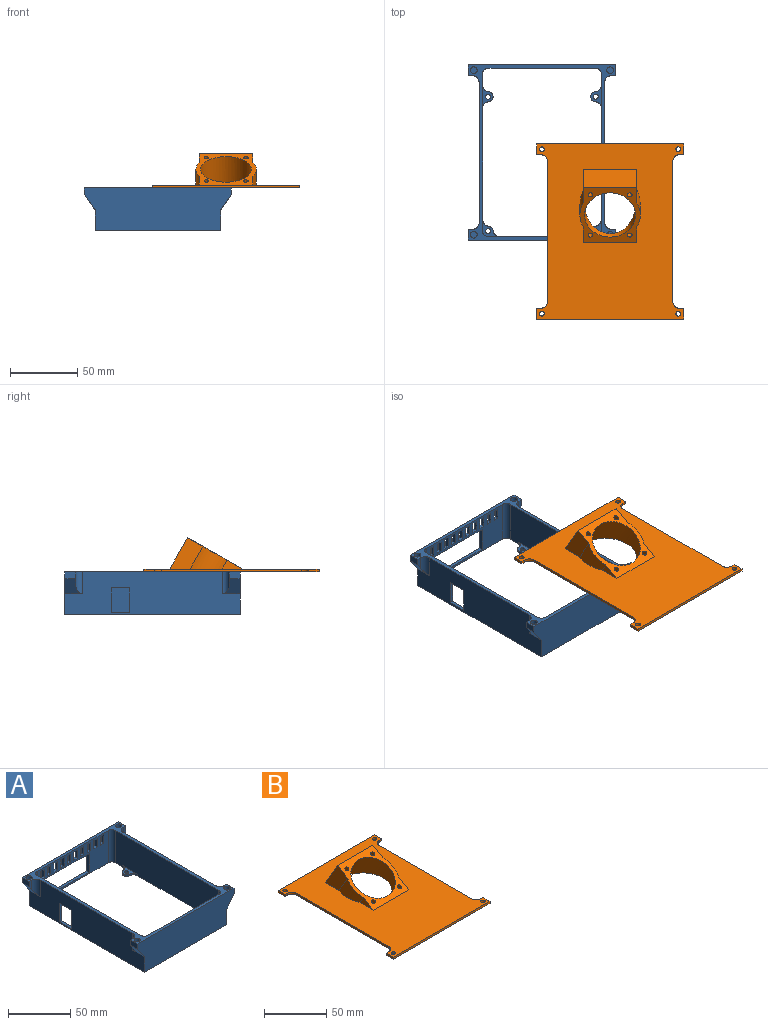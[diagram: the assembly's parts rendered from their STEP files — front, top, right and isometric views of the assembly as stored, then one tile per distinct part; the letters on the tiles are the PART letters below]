
ASSEMBLY  parts=2 mates=1
PART A: 106 faces, bbox 109.6x130.6x31.7 mm
  f0: plane 109.6x31.7mm, normal (0,1,0), area 1821.2mm2, adj f2,f3,f8,f9,f10,f13,f15,f16
  f1: plane 80.4x31.7mm, normal (0,-1,0), area 1231.3mm2, adj f8,f9,f10,f13,f15,f16,f62,f65
  f2: plane 130.6x31.7mm, normal (-1,0,0), area 3458.2mm2, adj f0,f6,f7,f9,f12,f14,f15,f20
  f3: plane 130.6x31.7mm, normal (1,0,0), area 3713mm2, adj f0,f9,f12,f15,f43,f53,f59,f61
  f4: plane 80.4x31.7mm, normal (0,1,0), area 2522.3mm2, adj f9,f15,f23,f26,f35,f37,f63,f64
  f5: plane 117.4x31.7mm, normal (1,0,0), area 3427.5mm2, adj f6,f7,f9,f14,f15,f19,f20,f23
  f6: plane 18.2x2.6mm, normal (0,-1,0), area 47.3mm2, adj f2,f5,f14,f20
  f7: plane 18.2x2.6mm, normal (0,1,0), area 47.3mm2, adj f2,f5,f14,f20
  f8: plane 18.2x2.6mm, normal (1,0,0), area 47.3mm2, adj f0,f1,f13,f16
  f9: plane 130.6x109.6mm, normal (0,0,1), area 1351.5mm2, adj f0,f1,f2,f3,f4,f5,f11,f12
  f10: plane 18.2x2.6mm, normal (-1,0,0), area 47.3mm2, adj f0,f1,f13,f16
  f11: plane 117.4x31.7mm, normal (-1,0,0), area 3682.3mm2, adj f9,f15,f26,f29,f30,f31,f34,f62
  f12: plane 109.6x31.7mm, normal (0,-1,0), area 3138.5mm2, adj f2,f3,f9,f15,f48,f49,f53,f54
  f13: plane 54.8x2.6mm, normal (0,0,-1), area 142.5mm2, adj f0,f1,f8,f10
  f14: plane 14x2.6mm, normal (0,0,-1), area 36.4mm2, adj f2,f5,f6,f7
  f15: plane 130.6x93.6mm, normal (0,0,-1), area 1366.8mm2, adj f0,f1,f2,f3,f4,f5,f11,f12
  f16: plane 54.8x2.6mm, normal (0,0,1), area 142.5mm2, adj f0,f1,f8,f10
  f17: cylinder r=3.75mm len=7.46mm, axis (0,0,-1), area 16.5mm2, adj f15,f19,f32,f33
  f18: cylinder r=1.85mm len=3.7mm, axis (0,0,-1), area 17.4mm2, adj f15,f19
  f19: plane 17.41x7.85mm, normal (0,0,1), area 52.4mm2, adj f5,f17,f18,f32,f33
  f20: plane 14x2.6mm, normal (0,0,1), area 36.4mm2, adj f2,f5,f6,f7
  f21: cylinder r=3.75mm len=3.34mm, axis (0,0,-1), area 7.7mm2, adj f15,f23,f36,f37
  f22: cylinder r=1.85mm len=3.7mm, axis (0,0,-1), area 17.4mm2, adj f15,f23
  f23: plane 12.8x12.8mm, normal (0,0,1), area 54.7mm2, adj f4,f5,f21,f22,f36,f37,f64
  f24: cylinder r=3.75mm len=3.34mm, axis (0,0,-1), area 7.7mm2, adj f15,f26,f34,f35
  f25: cylinder r=1.85mm len=3.7mm, axis (0,0,-1), area 17.4mm2, adj f15,f26
  f26: plane 12.8x12.8mm, normal (0,0,1), area 54.7mm2, adj f4,f11,f24,f25,f34,f35,f63
  f27: cylinder r=3.75mm len=7.46mm, axis (0,0,-1), area 16.5mm2, adj f15,f29,f30,f31
  f28: cylinder r=1.85mm len=3.7mm, axis (0,0,-1), area 17.4mm2, adj f15,f29
  f29: plane 17.41x7.85mm, normal (0,0,1), area 52.4mm2, adj f11,f27,f28,f30,f31
  f30: cylinder r=5mm len=4.97mm, axis (0,0,-1), area 11mm2, adj f11,f15,f27,f29
  f31: cylinder r=5mm len=4.97mm, axis (0,0,-1), area 11mm2, adj f11,f15,f27,f29
  f32: cylinder r=5mm len=4.97mm, axis (0,0,-1), area 11mm2, adj f5,f15,f17,f19
  f33: cylinder r=5mm len=4.97mm, axis (0,0,-1), area 11mm2, adj f5,f15,f17,f19
  f34: cylinder r=5mm len=4.97mm, axis (0,0,-1), area 11mm2, adj f11,f15,f24,f26
  f35: cylinder r=5mm len=4.97mm, axis (0,0,-1), area 11mm2, adj f4,f15,f24,f26
  f36: cylinder r=5mm len=4.97mm, axis (0,0,-1), area 11mm2, adj f5,f15,f21,f23
  f37: cylinder r=5mm len=4.97mm, axis (0,0,-1), area 11mm2, adj f4,f15,f21,f23
  f38: plane 13x11.43mm, normal (-0.82,0,-0.57), area 120.9mm2, adj f0,f2,f39,f40,f60
  f39: plane 8x5mm, normal (-1,0,0), area 40mm2, adj f0,f9,f38,f40
  f40: plane 9.28x3mm, normal (0,-1,0), area 21.4mm2, adj f9,f38,f39,f60
  f41: cylinder r=2.5mm len=6mm, axis (0,0,1), area 94.2mm2, adj f9,f42
  f42: plane 5x5mm, normal (0,0,1), area 19.6mm2, adj f41
  f43: plane 13x11.43mm, normal (0.82,0,-0.57), area 120.9mm2, adj f0,f3,f44,f45,f61
  f44: plane 8x5mm, normal (1,0,0), area 40mm2, adj f0,f9,f43,f45
  f45: plane 9.28x3mm, normal (0,-1,0), area 21.4mm2, adj f9,f43,f44,f61
  f46: cylinder r=2.5mm len=6mm, axis (0,0,1), area 94.2mm2, adj f9,f47
  f47: plane 5x5mm, normal (0,0,1), area 19.6mm2, adj f46
  f48: plane 13x11.43mm, normal (-0.82,0,-0.57), area 120.9mm2, adj f2,f12,f49,f50,f58
  f49: plane 8x5mm, normal (-1,0,0), area 40mm2, adj f9,f12,f48,f50
  f50: plane 9.28x3mm, normal (0,1,0), area 21.4mm2, adj f9,f48,f49,f58
  f51: cylinder r=2.5mm len=6mm, axis (0,0,1), area 94.2mm2, adj f9,f52
  f52: plane 5x5mm, normal (0,0,1), area 19.6mm2, adj f51
  f53: plane 13x11.43mm, normal (0.82,0,-0.57), area 120.9mm2, adj f3,f12,f54,f55,f59
  f54: plane 8x5mm, normal (1,0,0), area 40mm2, adj f9,f12,f53,f55
  f55: plane 9.28x3mm, normal (0,1,0), area 21.4mm2, adj f9,f53,f54,f59
  f56: cylinder r=2.5mm len=6mm, axis (0,0,1), area 94.2mm2, adj f9,f57
  f57: plane 5x5mm, normal (0,0,1), area 19.6mm2, adj f56
  f58: cylinder r=5mm len=16.43mm, axis (0,0,1), area 108.6mm2, adj f2,f9,f48,f50
  f59: cylinder r=5mm len=16.43mm, axis (0,0,1), area 108.6mm2, adj f3,f9,f53,f55
  f60: cylinder r=5mm len=16.43mm, axis (0,0,1), area 108.6mm2, adj f2,f9,f38,f40
  f61: cylinder r=5mm len=16.43mm, axis (0,0,1), area 108.6mm2, adj f3,f9,f43,f45
  f62: cylinder r=4mm len=31.7mm, axis (0,0,1), area 199.2mm2, adj f1,f9,f11,f15
  f63: cylinder r=4mm len=30.2mm, axis (0,0,1), area 189.8mm2, adj f4,f9,f11,f26
  f64: cylinder r=4mm len=30.2mm, axis (0,0,1), area 189.8mm2, adj f4,f5,f9,f23
  f65: cylinder r=4mm len=31.7mm, axis (0,0,1), area 199.2mm2, adj f1,f5,f9,f15
  f66: plane 8x2.6mm, normal (-1,0,0), area 20.8mm2, adj f0,f1,f67,f69
  f67: plane 4x2.6mm, normal (0,0,1), area 10.4mm2, adj f0,f1,f66,f68
  f68: plane 8x2.6mm, normal (1,0,0), area 20.8mm2, adj f0,f1,f67,f69
  f69: plane 4x2.6mm, normal (0,0,-1), area 10.4mm2, adj f0,f1,f66,f68
  f70: plane 8x2.6mm, normal (-1,0,0), area 20.8mm2, adj f0,f1,f71,f73
  f71: plane 4x2.6mm, normal (0,0,1), area 10.4mm2, adj f0,f1,f70,f72
  f72: plane 8x2.6mm, normal (1,0,0), area 20.8mm2, adj f0,f1,f71,f73
  f73: plane 4x2.6mm, normal (0,0,-1), area 10.4mm2, adj f0,f1,f70,f72
  f74: plane 8x2.6mm, normal (-1,0,0), area 20.8mm2, adj f0,f1,f75,f77
  f75: plane 4x2.6mm, normal (0,0,1), area 10.4mm2, adj f0,f1,f74,f76
  f76: plane 8x2.6mm, normal (1,0,0), area 20.8mm2, adj f0,f1,f75,f77
  f77: plane 4x2.6mm, normal (0,0,-1), area 10.4mm2, adj f0,f1,f74,f76
  f78: plane 4x2.6mm, normal (0,0,1), area 10.4mm2, adj f0,f1,f79,f81
  f79: plane 8x2.6mm, normal (1,0,0), area 20.8mm2, adj f0,f1,f78,f80
  f80: plane 4x2.6mm, normal (0,0,-1), area 10.4mm2, adj f0,f1,f79,f81
  f81: plane 8x2.6mm, normal (-1,0,0), area 20.8mm2, adj f0,f1,f78,f80
  f82: plane 8x2.6mm, normal (-1,0,0), area 20.8mm2, adj f0,f1,f83,f85
  f83: plane 4x2.6mm, normal (0,0,1), area 10.4mm2, adj f0,f1,f82,f84
  f84: plane 8x2.6mm, normal (1,0,0), area 20.8mm2, adj f0,f1,f83,f85
  f85: plane 4x2.6mm, normal (0,0,-1), area 10.4mm2, adj f0,f1,f82,f84
  f86: plane 8x2.6mm, normal (-1,0,0), area 20.8mm2, adj f0,f1,f87,f89
  f87: plane 4x2.6mm, normal (0,0,1), area 10.4mm2, adj f0,f1,f86,f88
  f88: plane 8x2.6mm, normal (1,0,0), area 20.8mm2, adj f0,f1,f87,f89
  f89: plane 4x2.6mm, normal (0,0,-1), area 10.4mm2, adj f0,f1,f86,f88
  f90: plane 8x2.6mm, normal (-1,0,0), area 20.8mm2, adj f0,f1,f91,f93
  f91: plane 4x2.6mm, normal (0,0,1), area 10.4mm2, adj f0,f1,f90,f92
  f92: plane 8x2.6mm, normal (1,0,0), area 20.8mm2, adj f0,f1,f91,f93
  f93: plane 4x2.6mm, normal (0,0,-1), area 10.4mm2, adj f0,f1,f90,f92
  f94: plane 8x2.6mm, normal (-1,0,0), area 20.8mm2, adj f0,f1,f95,f97
  f95: plane 4x2.6mm, normal (0,0,1), area 10.4mm2, adj f0,f1,f94,f96
  f96: plane 8x2.6mm, normal (1,0,0), area 20.8mm2, adj f0,f1,f95,f97
  f97: plane 4x2.6mm, normal (0,0,-1), area 10.4mm2, adj f0,f1,f94,f96
  f98: plane 8x2.6mm, normal (-1,0,0), area 20.8mm2, adj f0,f1,f99,f101
  f99: plane 4x2.6mm, normal (0,0,1), area 10.4mm2, adj f0,f1,f98,f100
  f100: plane 8x2.6mm, normal (1,0,0), area 20.8mm2, adj f0,f1,f99,f101
  f101: plane 4x2.6mm, normal (0,0,-1), area 10.4mm2, adj f0,f1,f98,f100
  f102: plane 8x2.6mm, normal (-1,0,0), area 20.8mm2, adj f0,f1,f103,f105
  f103: plane 4x2.6mm, normal (0,0,1), area 10.4mm2, adj f0,f1,f102,f104
  f104: plane 8x2.6mm, normal (1,0,0), area 20.8mm2, adj f0,f1,f103,f105
  f105: plane 4x2.6mm, normal (0,0,-1), area 10.4mm2, adj f0,f1,f102,f104
PART B: 39 faces, bbox 109.6x130.6x44.6 mm
  f0: plane 130.6x109.6mm, normal (0,0,-1), area 11141mm2, adj f5,f6,f7,f8,f9,f10,f11,f12
  f1: plane 45x40.64mm, normal (0,-0.5,0.87), area 774mm2, adj f2,f3,f4,f25,f26,f27,f28,f29
  f2: plane 130.6x109.6mm, normal (0,0,1), area 10215.3mm2, adj f1,f3,f4,f5,f6,f7,f8,f9
  f3: plane 15.19x6.58mm, normal (1,0,0), area 50mm2, adj f1,f2,f28
  f4: plane 15.19x6.58mm, normal (-1,0,0), area 50mm2, adj f1,f2,f29
  f5: plane 8x2mm, normal (1,0,0), area 16mm2, adj f0,f2,f6,f24
  f6: plane 109.6x2mm, normal (0,1,0), area 219.2mm2, adj f0,f2,f5,f7
  f7: plane 8x2mm, normal (-1,0,0), area 16mm2, adj f0,f2,f6,f8
  f8: plane 3x2mm, normal (0,-1,0), area 6mm2, adj f0,f2,f7,f9
  f9: cylinder r=5mm len=5mm, axis (0,0,-1), area 15.7mm2, adj f0,f2,f8,f10
  f10: plane 104.6x2mm, normal (-1,0,0), area 209.2mm2, adj f0,f2,f9,f11
  f11: cylinder r=5mm len=5mm, axis (0,0,-1), area 15.7mm2, adj f0,f2,f10,f12
  f12: plane 3x2mm, normal (0,1,0), area 6mm2, adj f0,f2,f11,f13
  f13: plane 8x2mm, normal (-1,0,0), area 16mm2, adj f0,f2,f12,f14
  f14: plane 109.6x2mm, normal (0,-1,0), area 219.2mm2, adj f0,f2,f13,f15
  f15: plane 8x2mm, normal (1,0,0), area 16mm2, adj f0,f2,f14,f16
  f16: plane 3x2mm, normal (0,1,0), area 6mm2, adj f0,f2,f15,f17
  f17: cylinder r=5mm len=5mm, axis (0,0,-1), area 15.7mm2, adj f0,f2,f16,f18
  f18: plane 104.6x2mm, normal (1,0,0), area 209.2mm2, adj f0,f2,f17,f19
  f19: cylinder r=5mm len=5mm, axis (0,0,-1), area 15.7mm2, adj f0,f2,f18,f24
  f20: cylinder r=1.75mm len=3.5mm, axis (0,0,-1), area 22mm2, adj f0,f2
  f21: cylinder r=1.75mm len=3.5mm, axis (0,0,-1), area 22mm2, adj f0,f2
  f22: cylinder r=1.75mm len=3.5mm, axis (0,0,-1), area 22mm2, adj f0,f2
  f23: cylinder r=1.75mm len=3.5mm, axis (0,0,-1), area 22mm2, adj f0,f2
  f24: plane 3x2mm, normal (0,-1,0), area 6mm2, adj f0,f2,f5,f19
  f25: plane 40x23.46mm, normal (0,0.87,0.5), area 1083.8mm2, adj f1,f2,f26,f27
  f26: plane 24.94x23.46mm, normal (1,0,0), area 306.5mm2, adj f1,f2,f25,f28
  f27: plane 24.94x23.46mm, normal (-1,0,0), area 306.5mm2, adj f1,f2,f25,f29
  f28: cylinder r=22.5mm len=27.6mm, axis (0,-0.5,0.87), area 290.1mm2, adj f1,f2,f3,f26
  f29: cylinder r=22.5mm len=27.6mm, axis (0,-0.5,0.87), area 290.1mm2, adj f1,f2,f4,f27
  f30: cylinder r=19mm len=46.4mm, axis (0,-0.5,0.87), area 1892.9mm2, adj f0,f1
  f31: cylinder r=1.75mm len=6.95mm, axis (0,-0.5,0.87), area 66mm2, adj f1,f32
  f32: plane 3.5x3.03mm, normal (0,-0.5,0.87), area 9.6mm2, adj f31
  f33: plane 3.48x1.36mm, normal (0,-0.5,0.87), area 4.2mm2, adj f0,f34
  f34: cylinder r=1.75mm len=6.95mm, axis (0,-0.5,0.87), area 61.8mm2, adj f0,f1,f33
  f35: plane 3.48x1.36mm, normal (0,-0.5,0.87), area 4.2mm2, adj f0,f36
  f36: cylinder r=1.75mm len=6.95mm, axis (0,-0.5,0.87), area 61.8mm2, adj f0,f1,f35
  f37: cylinder r=1.75mm len=6.95mm, axis (0,-0.5,0.87), area 66mm2, adj f1,f38
  f38: plane 3.5x3.03mm, normal (0,-0.5,0.87), area 9.6mm2, adj f37
PLACE A t=(-11.21,1.1,0.62)mm
PLACE B t=(39.59,-57.83,2.12)mm
MATE fastened B.f0 <-> A.f56  axis (0,0,-1) through (38.83,-58.36,30.62)mm
